# Revit family: 55-23-004 DN450-600
name_source: partatom
category: Pipe Accessories
units: mm (PartAtom-declared; Revit-internal decimal feet)

## family parameters
Always vertical = Yes
Cut with Voids When Loaded = No
Part Type = Valve - Breaks Into
Round Connector Dimension = Use Diameter
Shared = No
Work Plane-Based = No

## types (3) — shared parameters
1 = 1 mm  [stored 0.00328084 ft]
5 = 5 mm  [stored 0.0164042 ft]
Actuator_FL_D = 105 mm
Bonnet_dim1 = 78 mm
Bonnet_dim3 = 46 mm  [stored 0.150919 ft]
DN450_PN16 = 55-450-23-016640F1
DN500_PN16 = 55-500-23-016640F1
DN600_PN16 = 55-600-23-016640F1
Description_ = AVK GATE VALVE, FLANGED, UL/FM, ANSI CLASS 150, PN16
F1 = 19 mm
F2 = 50 mm  [stored 0.164042 ft]
F2_Height = 55 mm  [stored 0.180446 ft]
Rib1_R = 75 mm  [stored 0.246063 ft]
Search_table = 55-23-004 DN450-600
Stem = 20 mm  [stored 0.0656168 ft]
Stem4 = 25 mm  [stored 0.082021 ft]
URL_product_pages = https://www.avkvalves.com
stem1 = 25 mm  [stored 0.082021 ft]
stem2 = 38 mm
stem3 = 63 mm
zero-valued in all types: Default Elevation

## per-type parameters (varying)
- DN450_PN16: Body_Arc=1200 mm; Body_FL_L=377 mm; Body_FL_R=55 mm  [stored 0.180446 ft]; Body_FL_T=30 mm  [stored 0.0984252 ft]; Body_FL_W=168 mm; Body_FL_arc=1300 mm; Body_FL_rib_dim=1140 mm; Body_FL_rib_dim1=186 mm; Body_H=530 mm; Body_L=315 mm; Body_R=50 mm  [stored 0.164042 ft]; Body_T=15 mm  [stored 0.0492126 ft]; Body_W=93 mm; Body_bottom=285 mm; Body_rib_L=154 mm; Bonnet_L=299 mm; Bonnet_d1=90 mm  [stored 0.295276 ft]; Bonnet_d2=60 mm  [stored 0.19685 ft]; Bonnet_dim2=118 mm; Bore_R=225 mm; Bypass_L=252 mm; Bypass_R=30 mm  [stored 0.0984252 ft]; Bypass_W=135 mm; DN=450 mm; Dh=585 mm; Ds=31 mm  [stored 0.101706 ft]; F=16 mm  [stored 0.0524934 ft]; FL_R=320 mm; FL_T=30 mm  [stored 0.0984252 ft]; H=1170 mm; H3=1488 mm; H3-H=318 mm; Height1=995 mm; L=432 mm; OD=309 mm; RIB_L=418 mm; RIB_L1=272 mm; RIB_T=8 mm  [stored 0.0262467 ft]; Raised_R=260 mm; Raised_dis=4 mm  [stored 0.0131234 ft]; Rib1_H=430 mm; Rib1_L=590 mm; Rib1_T=11 mm  [stored 0.0360892 ft]; Rib1_W=340 mm; Rib2_H=300 mm; Rib2_L=590 mm; Rib2_W=340 mm; Rib3_H=180 mm; Rib3_L=590 mm; Rib3_W=340 mm; Rib4_H=25 mm  [stored 0.082021 ft]; Rib4_L=590 mm; Rib4_W=340 mm; Rib5_H=260 mm; Rib5_L=160 mm; Rib5_W=160 mm; Rib_T=26 mm; Sweep _cut=5 mm  [stored 0.0164042 ft]; W=419 mm; Wedge_L=79 mm; logo_H=265 mm
- DN500_PN16: Body_Arc=1200 mm; Body_FL_L=380 mm; Body_FL_R=60 mm  [stored 0.19685 ft]; Body_FL_T=33 mm; Body_FL_W=163 mm; Body_FL_arc=1350 mm; Body_FL_rib_dim=1166 mm; Body_FL_rib_dim1=197 mm; Body_H=560 mm; Body_L=340 mm; Body_R=50 mm  [stored 0.164042 ft]; Body_T=16 mm  [stored 0.0524934 ft]; Body_W=105 mm; Body_bottom=310 mm; Body_rib_L=172 mm; Bonnet_L=323 mm; Bonnet_d1=88 mm; Bonnet_d2=60 mm  [stored 0.19685 ft]; Bonnet_dim2=114 mm; Bore_R=250 mm; Bypass_L=272 mm; Bypass_R=45 mm  [stored 0.147638 ft]; Bypass_W=145 mm; DN=500 mm; Dh=650 mm; Ds=34 mm  [stored 0.111549 ft]; F=18 mm  [stored 0.0590551 ft]; FL_R=353 mm; FL_T=32 mm  [stored 0.104987 ft]; H=1196 mm; H3=1546 mm; H3-H=350 mm; Height1=1017 mm; L=457 mm; OD=345 mm; RIB_L=422 mm; RIB_L1=275 mm; RIB_T=8 mm  [stored 0.0262467 ft]; Raised_R=290 mm; Raised_dis=4 mm  [stored 0.0131234 ft]; Rib1_H=470 mm; Rib1_L=620 mm; Rib1_T=11 mm  [stored 0.0360892 ft]; Rib1_W=330 mm; Rib2_H=315 mm; Rib2_L=620 mm; Rib2_W=330 mm; Rib3_H=190 mm; Rib3_L=620 mm; Rib3_W=370 mm; Rib4_H=30 mm  [stored 0.0984252 ft]; Rib4_L=620 mm; Rib4_W=330 mm; Rib5_H=290 mm; Rib5_L=170 mm; Rib5_W=170 mm; Rib_T=28 mm; Sweep _cut=5 mm  [stored 0.0164042 ft]; W=423 mm; Wedge_L=89 mm; logo_H=280 mm
- DN600_PN16: Body_Arc=1222 mm; Body_FL_L=440 mm; Body_FL_R=65 mm  [stored 0.213255 ft]; Body_FL_T=35 mm  [stored 0.114829 ft]; Body_FL_W=178 mm; Body_FL_arc=1400 mm; Body_FL_rib_dim=1298 mm; Body_FL_rib_dim1=218 mm; Body_H=630 mm; Body_L=401 mm; Body_R=60 mm  [stored 0.19685 ft]; Body_T=17 mm  [stored 0.0557743 ft]; Body_W=130 mm; Body_bottom=371 mm; Body_rib_L=200 mm; Bonnet_L=381 mm; Bonnet_d1=108 mm; Bonnet_d2=75 mm  [stored 0.246063 ft]; Bonnet_dim2=125 mm; Bore_R=300 mm; Bypass_L=321 mm; Bypass_R=45 mm  [stored 0.147638 ft]; Bypass_W=179 mm; DN=600 mm; Dh=700 mm; Ds=35 mm  [stored 0.114829 ft]; F=16 mm  [stored 0.0524934 ft]; FL_R=430 mm; FL_T=36 mm  [stored 0.11811 ft]; H=1328 mm; H3=1736 mm; H3-H=408 mm; Height1=1129 mm; L=508 mm; OD=400 mm; RIB_L=488 mm; RIB_L1=318 mm; RIB_T=10 mm  [stored 0.0328084 ft]; Raised_R=360 mm; Raised_dis=5 mm  [stored 0.0164042 ft]; Rib1_H=495 mm; Rib1_L=720 mm; Rib1_T=13 mm  [stored 0.0426509 ft]; Rib1_W=360 mm; Rib2_H=330 mm; Rib2_L=720 mm; Rib2_W=360 mm; Rib3_H=210 mm; Rib3_L=720 mm; Rib3_W=360 mm; Rib4_H=35 mm  [stored 0.114829 ft]; Rib4_L=720 mm; Rib4_W=360 mm; Rib5_H=320 mm; Rib5_L=300 mm; Rib5_W=400 mm; Rib_T=31 mm  [stored 0.101706 ft]; Sweep _cut=6 mm  [stored 0.019685 ft]; W=489 mm; Wedge_L=111 mm; logo_H=315 mm

note: [stored X ft] marks values corroborated as IEEE doubles in the binary element streams (Revit-internal decimal feet)

## geometry (parser evidence)
native form markers: Sweep x7
no freeform markers — native parametric forms only
